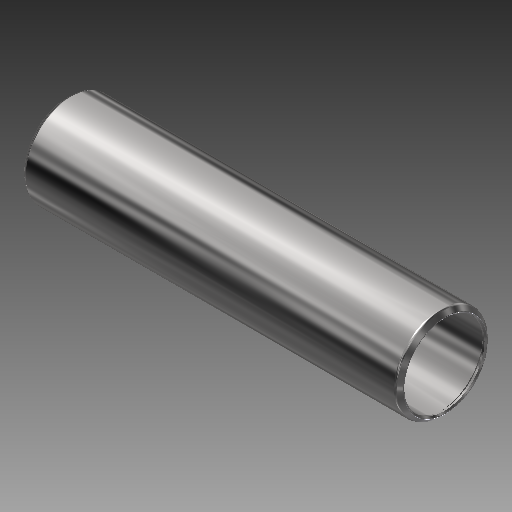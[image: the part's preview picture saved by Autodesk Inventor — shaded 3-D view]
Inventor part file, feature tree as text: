
AUTODESK INVENTOR PART (.ipt)
format: ipt  version: 2017 (Build 210142000, 142)  size: 210,432 bytes
history: native  units: in
note: dims shown in document units (in); Inventor stores cm internally (conversion verified against a paired STEP export)
features: other x42, revolve x1, sketch x1
ambient origin geometry x8: Origin, YZ Plane, XZ Plane, XY Plane, X Axis, Y Axis, Z Axis, Center Point
bodies: Solid1 (feature_tree)
feature tree (44):
  revolve  "Revolution1"  [1 undecoded]
  other  "cp1_XY"
  other  "cp1_YZ"
  other  "cp1_ZX"
  other  "cp1_X"
  other  "cp1_Y"
  other  "cp1_Z"
  other  "cp1_Center"
  other  "cp2_XY"
  other  "cp2_YZ"
  other  "cp2_ZX"
  other  "cp2_X"
  other  "cp2_Y"
  other  "cp2_Z"
  other  "cp2_Center"
  other  "cp3_XY"
  other  "cp3_YZ"
  other  "cp3_ZX"
  other  "cp3_X"
  other  "cp3_Y"
  other  "cp3_Z"
  other  "cp3_Center"
  other  "cp4_XY"
  other  "cp4_YZ"
  other  "cp4_ZX"
  other  "cp4_X"
  other  "cp4_Y"
  other  "cp4_Z"
  other  "cp4_Center"
  other  "tube_front_XY"
  other  "tube_front_YZ"
  other  "tube_front_ZX"
  other  "tube_front_X"
  other  "tube_front_Y"
  other  "tube_front_Z"
  other  "tube_front_Center"
  other  "tube_rear_XY"
  other  "tube_rear_YZ"
  other  "tube_rear_ZX"
  other  "tube_rear_X"
  other  "tube_rear_Y"
  other  "tube_rear_Z"
  other  "tube_rear_Center"
  sketch  "Sketch_1"  dims[d0=360.0deg]
note: 1 required parameter value undecoded (feature->parameter linkage not recoverable at this tier; creation-order binding heuristic only, values carry confidence <= 0.55)
